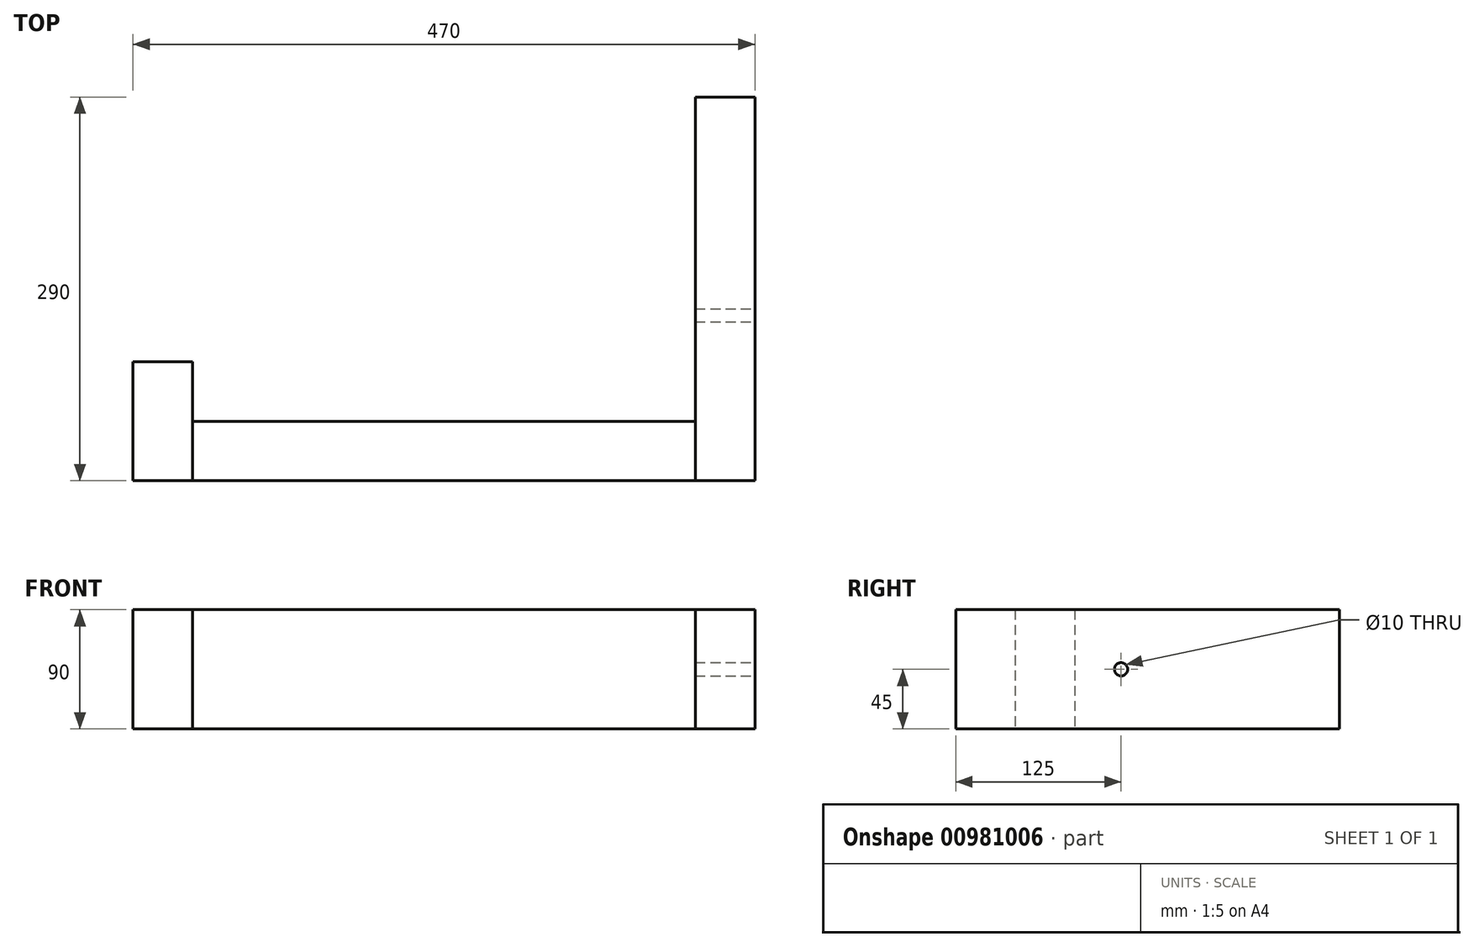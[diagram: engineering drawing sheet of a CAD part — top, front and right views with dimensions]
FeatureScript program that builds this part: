
annotation { "Feature Type Name" : "Feature", "Feature Type Description" : "" }
export const myFeature = defineFeature(function(context is Context, id is Id, definition is map)
    precondition{}
    {
        {
            var Q0;
            Q0=qCreatedBy(makeId("Top.planeOp"),FACE);
            var sketch = newSketch(context, id + "F0", { "sketchPlane" : qUnion([Q0])});
            skLineSegment(sketch, "E0.bottom", {"start": v(-235, 235) * mm, "end": v(235, 235) * mm});
            skLineSegment(sketch, "E0.top", {"start": v(-235, 190) * mm, "end": v(235, 190) * mm});
            skLineSegment(sketch, "E0.left", {"start": v(-235, 235) * mm, "end": v(-235, 190) * mm});
            skLineSegment(sketch, "E0.right", {"start": v(235, 235) * mm, "end": v(235, 190) * mm});
            skLineSegment(sketch, "E1.bottom", {"start": v(-190, 190) * mm, "end": v(-145, 190) * mm});
            skLineSegment(sketch, "E1.top", {"start": v(-190, -190) * mm, "end": v(-145, -190) * mm});
            skLineSegment(sketch, "E1.left", {"start": v(-190, 190) * mm, "end": v(-190, -190) * mm});
            skLineSegment(sketch, "E1.right", {"start": v(-145, 190) * mm, "end": v(-145, -190) * mm});
            skLineSegment(sketch, "E2.bottom", {"start": v(-190, -190) * mm, "end": v(190, -190) * mm});
            skLineSegment(sketch, "E2.top", {"start": v(-190, -235) * mm, "end": v(190, -235) * mm});
            skLineSegment(sketch, "E2.left", {"start": v(-190, -190) * mm, "end": v(-190, -235) * mm});
            skLineSegment(sketch, "E2.right", {"start": v(190, -190) * mm, "end": v(190, -235) * mm});
            skLineSegment(sketch, "E3.bottom", {"start": v(190, -235) * mm, "end": v(235, -235) * mm});
            skLineSegment(sketch, "E3.top", {"start": v(190, 55) * mm, "end": v(235, 55) * mm});
            skLineSegment(sketch, "E3.left", {"start": v(190, -235) * mm, "end": v(190, 55) * mm});
            skLineSegment(sketch, "E3.right", {"start": v(235, -235) * mm, "end": v(235, 55) * mm});
            skLineSegment(sketch, "E4.top", {"start": v(190, 190) * mm, "end": v(235, 190) * mm});
            skLineSegment(sketch, "E4.left", {"start": v(190, 55) * mm, "end": v(190, 190) * mm});
            skLineSegment(sketch, "E4.right", {"start": v(235, 55) * mm, "end": v(235, 190) * mm});
            skLineSegment(sketch, "E5.bottom", {"start": v(-190, -235) * mm, "end": v(-235, -235) * mm});
            skLineSegment(sketch, "E5.top", {"start": v(-190, -145) * mm, "end": v(-235, -145) * mm});
            skLineSegment(sketch, "E5.left", {"start": v(-190, -235) * mm, "end": v(-190, -145) * mm});
            skLineSegment(sketch, "E5.right", {"start": v(-235, -235) * mm, "end": v(-235, -145) * mm});
            skLineSegment(sketch, "E6.bottom", {"start": v(90, -45) * mm, "end": v(135, -45) * mm});
            skLineSegment(sketch, "E6.top", {"start": v(90, -135) * mm, "end": v(135, -135) * mm});
            skLineSegment(sketch, "E6.left", {"start": v(90, -45) * mm, "end": v(90, -135) * mm});
            skLineSegment(sketch, "E6.right", {"start": v(135, -45) * mm, "end": v(135, -135) * mm});
            skLineSegment(sketch, "E7", {"start": v(0, 235) * mm, "end": v(0, 0) * mm, "construction": true});
            skSolve(sketch);
        }
        {
            var Q0;
            Q0=makeQuery(id+"F0.imprint","IMPRINT",FACE,{"disambiguationData":[TD([[makeQuery(id+"F0.imprint","IMPRINT",EDGE,{"derivedFrom":sQuery(id+"F0.wireOp",EDGE,"E2.right")}),1.0]])]});
            extrude(context, id + "F1", {"entities" : qUnion([Q0]), "depth" : 90 * mm, "offsetDistance" : 25 * mm});
        }
        {
            var Q0;
            Q0=makeQuery(id+"F0.imprint","IMPRINT",FACE,{"disambiguationData":[TD([[makeQuery(id+"F0.imprint","IMPRINT",EDGE,{"derivedFrom":sQuery(id+"F0.wireOp",EDGE,"E1.top")}),-1.0]])]});
            extrude(context, id + "F2", {"entities" : qUnion([Q0]), "depth" : 90 * mm, "offsetDistance" : 25 * mm});
        }
        {
            var Q0;
            {var subQ1=sQuery(id+"F0.wireOp",EDGE,"E2.left");Q0=makeQuery(id+"F0.imprint","IMPRINT",FACE,{"disambiguationData":[TD([[makeQuery(id+"F0.imprint","IMPRINT",EDGE,{"derivedFrom":subQ1}),-1.0]])]});}
            extrude(context, id + "F3", {"entities" : qUnion([Q0]), "depth" : 90 * mm, "offsetDistance" : 25 * mm});
        }
        {
            var Q0;
            Q0=makeQuery(id+"F1.opExtrude","SWEPT_FACE",FACE,{"disambiguationData":[OSD([sQuery(id+"F0.wireOp",EDGE,"E3.right")])]});
            var sketch = newSketch(context, id + "F4", { "sketchPlane" : qUnion([Q0])});
            skCircle(sketch, "E8", {"center": v(-110, 45) * mm, "radius": 5 * mm});
            skLineSegment(sketch, "E9", {"start": v(-110, 45) * mm, "end": v(-235, 45) * mm, "construction": true});
            skSolve(sketch);
        }
        {
            var Q0;
            Q0 = qSketchRegion(id + "F4", true);
            extrude(context, id + "F5", {"entities" : qUnion([Q0]), "operationType" : NewBodyOperationType.REMOVE, "endBound" : BoundingType.UP_TO_NEXT, "oppositeDirection" : true, "depth" : 25 * mm, "offsetDistance" : 25 * mm});
        }
    });
